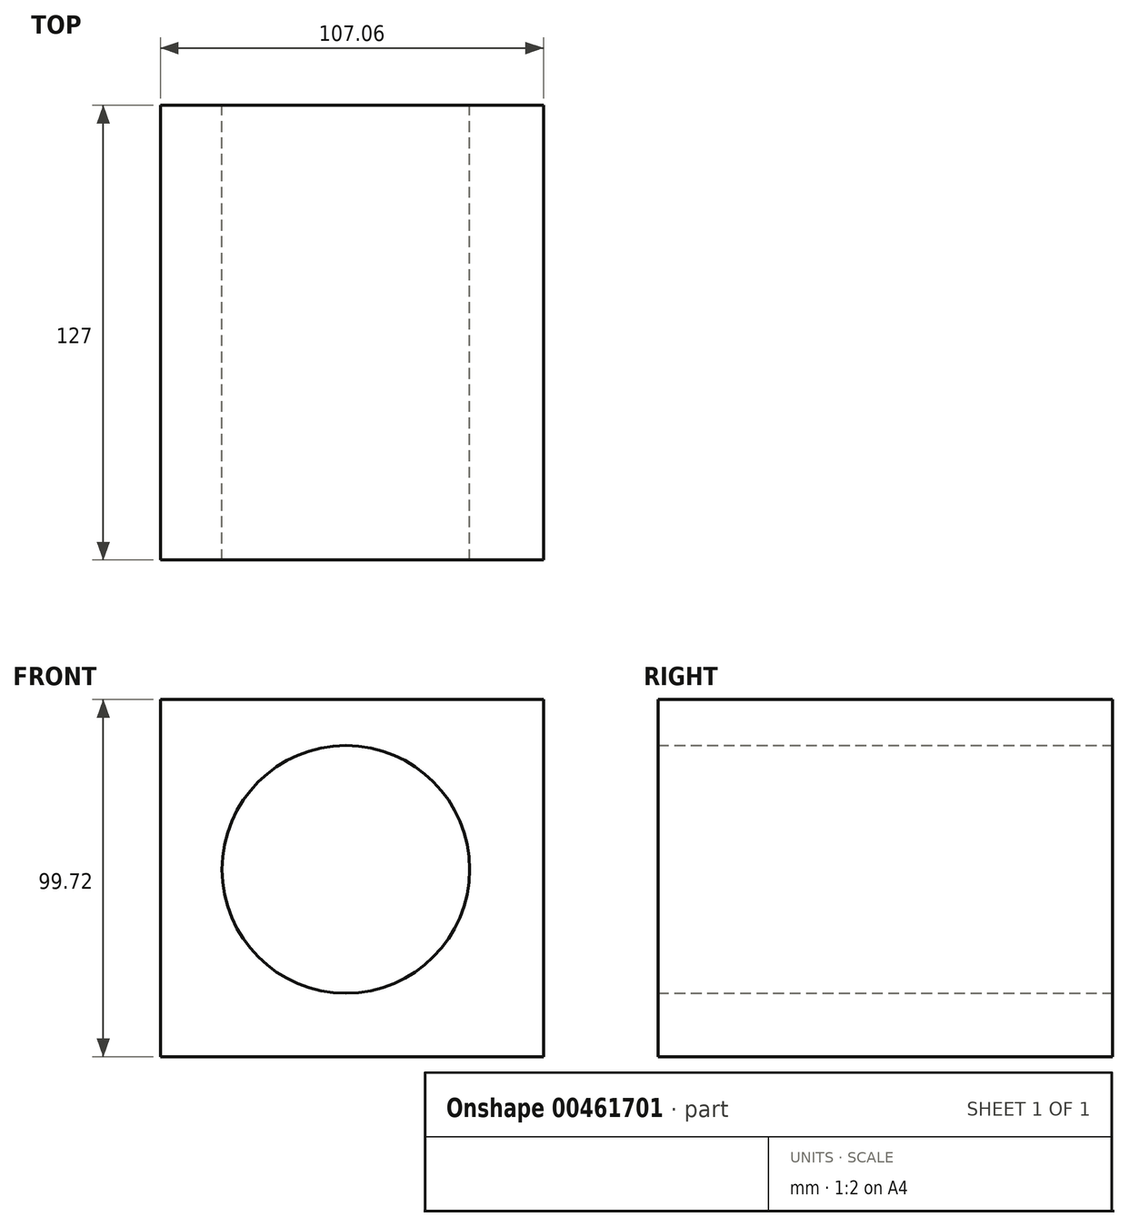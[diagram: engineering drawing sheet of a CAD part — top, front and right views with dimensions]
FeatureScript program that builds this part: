
annotation { "Feature Type Name" : "Feature", "Feature Type Description" : "" }
export const myFeature = defineFeature(function(context is Context, id is Id, definition is map)
    precondition{}
    {
        {
            var Q0;
            Q0=qCreatedBy(makeId("Front.planeOp"),FACE);
            var sketch = newSketch(context, id + "F0", { "sketchPlane" : qUnion([Q0])});
            skLineSegment(sketch, "E0.bottom", {"start": v(55.24, 47.42) * mm, "end": v(-51.82, 47.42) * mm});
            skLineSegment(sketch, "E0.top", {"start": v(55.24, -52.3) * mm, "end": v(-51.82, -52.3) * mm});
            skLineSegment(sketch, "E0.left", {"start": v(55.24, 47.42) * mm, "end": v(55.24, -52.3) * mm});
            skLineSegment(sketch, "E0.right", {"start": v(-51.82, 47.42) * mm, "end": v(-51.82, -52.3) * mm});
            skCircle(sketch, "E1", {"center": v(0, 0) * mm, "radius": 34.6 * mm});
            skSolve(sketch);
        }
        {
            var Q0;
            Q0=makeQuery(id+"F0.imprint","IMPRINT",FACE,{"disambiguationData":[TD([[makeQuery(id+"F0.imprint","IMPRINT",EDGE,{"derivedFrom":sQuery(id+"F0.wireOp",EDGE,"E0.bottom")}),1.0]])]});
            extrude(context, id + "F1", {"entities" : qUnion([Q0]), "depth" : 127 * mm});
        }
    });
